# Revit family: TCNHBLE_with_1X2_Mixing_Box
name_source: partatom
category: Mechanical Equipment
units: mm (PartAtom-declared; Revit-internal decimal feet)

## family parameters
Always vertical = Yes
Cut with Voids When Loaded = No
Part Type = Normal
Room Calculation Point = No
Round Connector Dimension = Use Diameter
Shared = No
Work Plane-Based = No

## types (34) — shared parameters
0 = 0"
1" = 1"
1.5 = 1 1/2"
135 = 135.00°
2" = 2"
2' = 24"
3" = 3"
3.125" = 3 1/8"
4" = 4"
5" = 5"
Manufacturer = Loren Cook Company
Model = TCNHBLE-1X2_Mixing Box
ONE EIGTH = 1/8"
Type Comments = Tubular Centrifugal Inline Upblast Roof Mounted Arrangement 9 With 1X2 Mixing Box
URL = www.lorencook.com

## per-type parameters (varying)
- 100_TCNHBLE_1x2_ENDS: ((E - MIXING_BOX_HEIGHT - 0'  5") * 0.8)=19 19/32"; (C/2)+.125"=12 1/8"; (C/2)+.5"=-11 1/2"; (C/2)-.5"=-12 1/2"; -((E - MIXING_BOX_HEIGHT - 0'  5") * 0.8)=-19 19/32"; -B=-23 1/16"; -B/2=-11 17/32"; -C=-24"; A=120"; A-C-D=41"; B=23 1/16"; B/2=11 17/32"; C=24"; C+.25"=24 1/4"; C/2=30"; D=34"; DUAL_F=51"; DUAL_F+.5"=51 1/2"; DUAL_F/2=25 1/2"; E=60"; F=20"; F-1"=19"; FAN_DIA=16"; FAN_DIA-(C/2)=4"; FAN_RAD=8"; FAN_RAD*.33=5 9/32"; FAN_RAD*.8=4 13/16"; FAN_RAD+4"=12"; LONG_RO=44 1/16"; MB/2=15 1/4"; MIXING_BOX_HEIGHT=30 1/2"; MIXING_BOX_HEIGHT+.125"=30 5/8"; MIXING_BOX_HEIGHT-2.875"=27 5/8"; RO=16 13/16"; RO/2=8 13/32"; TYPE=12"
- 120_TCNHBLE_1x2_ENDS: ((E - MIXING_BOX_HEIGHT - 0'  5") * 0.8)=20 13/32"; (C/2)+.125"=14 1/8"; (C/2)+.5"=-13 1/2"; (C/2)-.5"=-14 1/2"; -((E - MIXING_BOX_HEIGHT - 0'  5") * 0.8)=-20 13/32"; -B=-27 1/16"; -B/2=-13 17/32"; -C=-28"; A=120"; A-C-D=37"; B=27 1/16"; B/2=13 17/32"; C=28"; C+.25"=28 1/4"; C/2=31"; D=38"; DUAL_F=59"; DUAL_F+.5"=59 1/2"; DUAL_F/2=29 1/2"; E=62"; F=22"; F-1"=21"; FAN_DIA=18"; FAN_DIA-(C/2)=4"; FAN_RAD=9"; FAN_RAD*.33=5 15/16"; FAN_RAD*.8=5 13/32"; FAN_RAD+4"=13"; LONG_RO=52 1/16"; MB/2=15 3/4"; MIXING_BOX_HEIGHT=31 1/2"; MIXING_BOX_HEIGHT+.125"=31 5/8"; MIXING_BOX_HEIGHT-2.875"=28 5/8"; RO=20 13/16"; RO/2=10 13/32"; TYPE=12"
- 135_TCNHBLE_1x2_ENDS: ((E - MIXING_BOX_HEIGHT - 0'  5") * 0.8)=21"; (C/2)+.125"=15 1/8"; (C/2)+.5"=-14 1/2"; (C/2)-.5"=-15 1/2"; -((E - MIXING_BOX_HEIGHT - 0'  5") * 0.8)=-21"; -B=-29"; -B/2=-14 1/2"; -C=-30"; A=120"; A-C-D=32"; B=29"; B/2=14 1/2"; C=30"; C+.25"=30 1/4"; C/2=31 1/2"; D=40"; DUAL_F=63"; DUAL_F+.5"=63 1/2"; DUAL_F/2=31 1/2"; E=63"; F=26"; F-1"=25"; FAN_DIA=21"; FAN_DIA-(C/2)=6"; FAN_RAD=10 1/2"; FAN_RAD*.33=6 15/16"; FAN_RAD*.8=6 5/16"; FAN_RAD+4"=14 1/2"; LONG_RO=56 1/16"; MB/2=15 7/8"; MIXING_BOX_HEIGHT=31 3/4"; MIXING_BOX_HEIGHT+.125"=31 7/8"; MIXING_BOX_HEIGHT-2.875"=28 7/8"; RO=22 3/4"; RO/2=11 3/8"; TYPE=12"
- 150_TCNHBLE_1x2_ENDS: ((E - MIXING_BOX_HEIGHT - 0'  5") * 0.8)=23 19/32"; (C/2)+.125"=16 1/8"; (C/2)+.5"=-15 1/2"; (C/2)-.5"=-16 1/2"; -((E - MIXING_BOX_HEIGHT - 0'  5") * 0.8)=-23 19/32"; -B=-31"; -B/2=-15 1/2"; -C=-32"; A=120"; A-C-D=25"; B=31"; B/2=15 1/2"; C=32"; C+.25"=32 1/4"; C/2=33 1/2"; D=42"; DUAL_F=67"; DUAL_F+.5"=67 1/2"; DUAL_F/2=33 1/2"; E=67"; F=29"; F-1"=28"; FAN_DIA=24"; FAN_DIA-(C/2)=8"; FAN_RAD=12"; FAN_RAD*.33=7 29/32"; FAN_RAD*.8=7 3/16"; FAN_RAD+4"=16"; LONG_RO=60 1/16"; MB/2=16 1/4"; MIXING_BOX_HEIGHT=32 1/2"; MIXING_BOX_HEIGHT+.125"=32 5/8"; MIXING_BOX_HEIGHT-2.875"=29 5/8"; RO=24 3/4"; RO/2=12 3/8"; TYPE=12"
- 165_TCNHBLE_1x2_ENDS: ((E - MIXING_BOX_HEIGHT - 0'  5") * 0.8)=24 13/16"; (C/2)+.125"=17 1/8"; (C/2)+.5"=-16 1/2"; (C/2)-.5"=-17 1/2"; -((E - MIXING_BOX_HEIGHT - 0'  5") * 0.8)=-24 13/16"; -B=-33"; -B/2=-16 1/2"; -C=-34"; A=120"; A-C-D=21"; B=33"; B/2=16 1/2"; C=34"; C+.25"=34 1/4"; C/2=35"; D=46"; DUAL_F=71"; DUAL_F+.5"=71 1/2"; DUAL_F/2=35 1/2"; E=70"; F=30"; F-1"=29"; FAN_DIA=26"; FAN_DIA-(C/2)=9"; FAN_RAD=13"; FAN_RAD*.33=8 19/32"; FAN_RAD*.8=7 13/16"; FAN_RAD+4"=17"; LONG_RO=64 1/16"; MB/2=17"; MIXING_BOX_HEIGHT=34"; MIXING_BOX_HEIGHT+.125"=34 1/8"; MIXING_BOX_HEIGHT-2.875"=31 1/8"; RO=26 3/4"; RO/2=13 3/8"; TYPE=12"
- 180_TCNHBLE_1x2_ENDS: ((E - MIXING_BOX_HEIGHT - 0'  5") * 0.8)=26 13/32"; (C/2)+.125"=19 1/8"; (C/2)+.5"=-18 1/2"; (C/2)-.5"=-19 1/2"; -((E - MIXING_BOX_HEIGHT - 0'  5") * 0.8)=-26 13/32"; -B=-36 7/8"; -B/2=-18 7/16"; -C=-38"; A=120"; A-C-D=13"; B=36 7/8"; B/2=18 7/16"; C=38"; C+.25"=38 1/4"; C/2=36 1/2"; D=50"; DUAL_F=79"; DUAL_F+.5"=79 1/2"; DUAL_F/2=39 1/2"; E=73"; F=35"; F-1"=34"; FAN_DIA=28"; FAN_DIA-(C/2)=9"; FAN_RAD=14"; FAN_RAD*.33=9 1/4"; FAN_RAD*.8=8 13/32"; FAN_RAD+4"=18"; LONG_RO=71 13/16"; MB/2=17 1/2"; MIXING_BOX_HEIGHT=35"; MIXING_BOX_HEIGHT+.125"=35 1/8"; MIXING_BOX_HEIGHT-2.875"=32 1/8"; RO=30 5/8"; RO/2=15 5/16"; TYPE=12"
- 195_TCNHBLE_1x2_ENDS: ((E - MIXING_BOX_HEIGHT - 0'  5") * 0.8)=28 3/16"; (C/2)+.125"=21 1/8"; (C/2)+.5"=-20 1/2"; (C/2)-.5"=-21 1/2"; -((E - MIXING_BOX_HEIGHT - 0'  5") * 0.8)=-28 3/16"; -B=-40 7/8"; -B/2=-20 7/16"; -C=-42"; A=120"; A-C-D=6"; B=40 7/8"; B/2=20 7/16"; C=42"; C+.25"=42 1/4"; C/2=38"; D=54"; DUAL_F=87"; DUAL_F+.5"=87 1/2"; DUAL_F/2=43 1/2"; E=76"; F=39"; F-1"=38"; FAN_DIA=31"; FAN_DIA-(C/2)=10"; FAN_RAD=15 1/2"; FAN_RAD*.33=10 7/32"; FAN_RAD*.8=9 5/16"; FAN_RAD+4"=19 1/2"; LONG_RO=79 15/16"; MB/2=17 7/8"; MIXING_BOX_HEIGHT=35 3/4"; MIXING_BOX_HEIGHT+.125"=35 7/8"; MIXING_BOX_HEIGHT-2.875"=32 7/8"; RO=34 11/16"; RO/2=17 11/32"; TYPE=12"
- 210_TCNHBLE_1x2_ENDS: ((E - MIXING_BOX_HEIGHT - 0'  5") * 0.8)=29 3/16"; (C/2)+.125"=22 1/8"; (C/2)+.5"=-21 1/2"; (C/2)-.5"=-22 1/2"; -((E - MIXING_BOX_HEIGHT - 0'  5") * 0.8)=-29 3/16"; -B=-42 7/8"; -B/2=-21 7/16"; -C=-44"; A=124"; A-C-D=7"; B=42 7/8"; B/2=21 7/16"; C=44"; C+.25"=44 1/4"; C/2=38"; D=56"; DUAL_F=91"; DUAL_F+.5"=91 1/2"; DUAL_F/2=45 1/2"; E=76"; F=42"; F-1"=41"; FAN_DIA=34"; FAN_DIA-(C/2)=12"; FAN_RAD=17"; FAN_RAD*.33=11 7/32"; FAN_RAD*.8=10 3/16"; FAN_RAD+4"=21"; LONG_RO=83 15/16"; MB/2=17 1/4"; MIXING_BOX_HEIGHT=34 1/2"; MIXING_BOX_HEIGHT+.125"=34 5/8"; MIXING_BOX_HEIGHT-2.875"=31 5/8"; RO=36 11/16"; RO/2=18 11/32"; TYPE=12"
- 225_TCNHBLE_1x2_ENDS: ((E - MIXING_BOX_HEIGHT - 0'  5") * 0.8)=30 3/16"; (C/2)+.125"=24 1/8"; (C/2)+.5"=-23 1/2"; (C/2)-.5"=-24 1/2"; -((E - MIXING_BOX_HEIGHT - 0'  5") * 0.8)=-30 3/16"; -B=-46 7/8"; -B/2=-23 7/16"; -C=-48"; A=121 1/2"; A-C-D=1/2"; B=46 7/8"; B/2=23 7/16"; C=48"; C+.25"=48 1/4"; C/2=39"; D=60"; DUAL_F=99"; DUAL_F+.5"=99 1/2"; DUAL_F/2=49 1/2"; E=78"; F=44"; F-1"=43"; FAN_DIA=36"; FAN_DIA-(C/2)=12"; FAN_RAD=18"; FAN_RAD*.33=11 7/8"; FAN_RAD*.8=10 13/16"; FAN_RAD+4"=22"; LONG_RO=91 15/16"; MB/2=17 5/8"; MIXING_BOX_HEIGHT=35 1/4"; MIXING_BOX_HEIGHT+.125"=35 3/8"; MIXING_BOX_HEIGHT-2.875"=32 3/8"; RO=40 11/16"; RO/2=20 11/32"; TYPE=12"
- 245_TCNHBLE_1x2_ENDS: ((E - MIXING_BOX_HEIGHT - 0'  5") * 0.8)=34"; (C/2)+.125"=25 1/8"; (C/2)+.5"=-24 1/2"; (C/2)-.5"=-25 1/2"; -((E - MIXING_BOX_HEIGHT - 0'  5") * 0.8)=-34"; -B=-48 7/8"; -B/2=-24 7/16"; -C=-50"; A=135"; A-C-D=1"; B=48 7/8"; B/2=24 7/16"; C=50"; C+.25"=50 1/4"; C/2=42 1/2"; D=63"; DUAL_F=103"; DUAL_F+.5"=103 1/2"; DUAL_F/2=51 1/2"; E=85"; F=50"; F-1"=49"; FAN_DIA=40"; FAN_DIA-(C/2)=15"; FAN_RAD=20"; FAN_RAD*.33=13 3/16"; FAN_RAD*.8=12"; FAN_RAD+4"=24"; LONG_RO=95 15/16"; MB/2=18 3/4"; MIXING_BOX_HEIGHT=37 1/2"; MIXING_BOX_HEIGHT+.125"=37 5/8"; MIXING_BOX_HEIGHT-2.875"=34 5/8"; RO=42 11/16"; RO/2=21 11/32"; TYPE=12"
- 270_TCNHBLE_1x2_ENDS: ((E - MIXING_BOX_HEIGHT - 0'  5") * 0.8)=38 13/16"; (C/2)+.125"=27 1/8"; (C/2)+.5"=-26 1/2"; (C/2)-.5"=-27 1/2"; -((E - MIXING_BOX_HEIGHT - 0'  5") * 0.8)=-38 13/16"; -B=-52 7/8"; -B/2=-26 7/16"; -C=-54"; A=146 3/4"; A-C-D=3/4"; B=52 7/8"; B/2=26 7/16"; C=54"; C+.25"=54 1/4"; C/2=45 1/2"; D=67"; DUAL_F=111"; DUAL_F+.5"=111 1/2"; DUAL_F/2=55 1/2"; E=91"; F=56"; F-1"=55"; FAN_DIA=44"; FAN_DIA-(C/2)=17"; FAN_RAD=22"; FAN_RAD*.33=14 17/32"; FAN_RAD*.8=13 3/16"; FAN_RAD+4"=26"; LONG_RO=103 15/16"; MB/2=18 3/4"; MIXING_BOX_HEIGHT=37 1/2"; MIXING_BOX_HEIGHT+.125"=37 5/8"; MIXING_BOX_HEIGHT-2.875"=34 5/8"; RO=46 11/16"; RO/2=23 11/32"; TYPE=12"
- 300_TCNHBLE_1x2_ENDS: ((E - MIXING_BOX_HEIGHT - 0'  5") * 0.8)=39 13/16"; (C/2)+.125"=30 1/8"; (C/2)+.5"=-29 1/2"; (C/2)-.5"=-30 1/2"; -((E - MIXING_BOX_HEIGHT - 0'  5") * 0.8)=-39 13/16"; -B=-58 7/8"; -B/2=-29 7/16"; -C=-60"; A=153"; A-C-D=1"; B=58 7/8"; B/2=29 7/16"; C=60"; C+.25"=60 1/4"; C/2=46 1/2"; D=74"; DUAL_F=123"; DUAL_F+.5"=123 1/2"; DUAL_F/2=61 1/2"; E=93"; F=60"; F-1"=59"; FAN_DIA=48"; FAN_DIA-(C/2)=18"; FAN_RAD=24"; FAN_RAD*.33=15 27/32"; FAN_RAD*.8=14 13/32"; FAN_RAD+4"=28"; LONG_RO=115 15/16"; MB/2=19 1/8"; MIXING_BOX_HEIGHT=38 1/4"; MIXING_BOX_HEIGHT+.125"=38 3/8"; MIXING_BOX_HEIGHT-2.875"=35 3/8"; RO=52 11/16"; RO/2=26 11/32"; TYPE=12"
- 330_TCNHBLE_1x2_ENDS: ((E - MIXING_BOX_HEIGHT - 0'  5") * 0.8)=42 13/16"; (C/2)+.125"=31 1/8"; (C/2)+.5"=-30 1/2"; (C/2)-.5"=-31 1/2"; -((E - MIXING_BOX_HEIGHT - 0'  5") * 0.8)=-42 13/16"; -B=-60 3/4"; -B/2=-30 3/8"; -C=-62"; A=164 1/4"; A-C-D=1 1/4"; B=60 3/4"; B/2=30 3/8"; C=62"; C+.25"=62 1/4"; C/2=50"; D=77"; DUAL_F=127"; DUAL_F+.5"=127 1/2"; DUAL_F/2=63 1/2"; E=100"; F=64"; F-1"=63"; FAN_DIA=52"; FAN_DIA-(C/2)=21"; FAN_RAD=26"; FAN_RAD*.33=17 5/32"; FAN_RAD*.8=15 19/32"; FAN_RAD+4"=30"; LONG_RO=119 13/16"; MB/2=20 3/4"; MIXING_BOX_HEIGHT=41 1/2"; MIXING_BOX_HEIGHT+.125"=41 5/8"; MIXING_BOX_HEIGHT-2.875"=38 5/8"; RO=54 9/16"; RO/2=27 9/32"; TYPE=12"
- 365_TCNHBLE_1x2_ENDS: ((E - MIXING_BOX_HEIGHT - 0'  5") * 0.8)=44 19/32"; (C/2)+.125"=32 5/8"; (C/2)+.5"=-32"; (C/2)-.5"=-33"; -((E - MIXING_BOX_HEIGHT - 0'  5") * 0.8)=-44 19/32"; -B=-63 3/4"; -B/2=-31 7/8"; -C=-65"; A=170"; A-C-D=1"; B=63 3/4"; B/2=31 7/8"; C=65"; C+.25"=65 1/4"; C/2=52 1/2"; D=82"; DUAL_F=133"; DUAL_F+.5"=133 1/2"; DUAL_F/2=66 1/2"; E=105"; F=65"; F-1"=64"; FAN_DIA=54"; FAN_DIA-(C/2)=21 1/2"; FAN_RAD=27"; FAN_RAD*.33=17 13/16"; FAN_RAD*.8=16 3/16"; FAN_RAD+4"=31"; LONG_RO=125 13/16"; MB/2=22 1/8"; MIXING_BOX_HEIGHT=44 1/4"; MIXING_BOX_HEIGHT+.125"=44 3/8"; MIXING_BOX_HEIGHT-2.875"=41 3/8"; RO=57 9/16"; RO/2=28 25/32"; TYPE=12"
- 402_TCNHBLE_1x2_ENDS: ((E - MIXING_BOX_HEIGHT - 0'  5") * 0.8)=49 3/16"; (C/2)+.125"=36 1/8"; (C/2)+.5"=-35 1/2"; (C/2)-.5"=-36 1/2"; -((E - MIXING_BOX_HEIGHT - 0'  5") * 0.8)=-49 3/16"; -B=-70 3/4"; -B/2=-35 3/8"; -C=-72"; A=184 3/4"; A-C-D=3/4"; B=70 3/4"; B/2=35 3/8"; C=72"; C+.25"=72 1/4"; C/2=56 1/2"; D=90"; DUAL_F=147"; DUAL_F+.5"=147 1/2"; DUAL_F/2=73 1/2"; E=113"; F=72"; F-1"=71"; FAN_DIA=60"; FAN_DIA-(C/2)=24"; FAN_RAD=30"; FAN_RAD*.33=19 13/16"; FAN_RAD*.8=18"; FAN_RAD+4"=34"; LONG_RO=139 13/16"; MB/2=23 1/4"; MIXING_BOX_HEIGHT=46 1/2"; MIXING_BOX_HEIGHT+.125"=46 5/8"; MIXING_BOX_HEIGHT-2.875"=43 5/8"; RO=64 9/16"; RO/2=32 9/32"; TYPE=12"
- 445_TCNHBLE_1x2_ENDS: ((E - MIXING_BOX_HEIGHT - 0'  5") * 0.8)=54 3/16"; (C/2)+.125"=38 5/8"; (C/2)+.5"=-38"; (C/2)-.5"=-39"; -((E - MIXING_BOX_HEIGHT - 0'  5") * 0.8)=-54 3/16"; -B=-75 3/4"; -B/2=-37 7/8"; -C=-77"; A=206"; A-C-D=1"; B=75 3/4"; B/2=37 7/8"; C=77"; C+.25"=77 1/4"; C/2=63"; D=98"; DUAL_F=157"; DUAL_F+.5"=157 1/2"; DUAL_F/2=78 1/2"; E=126"; F=80"; F-1"=79"; FAN_DIA=66"; FAN_DIA-(C/2)=27 1/2"; FAN_RAD=33"; FAN_RAD*.33=21 25/32"; FAN_RAD*.8=19 13/16"; FAN_RAD+4"=37"; LONG_RO=149 13/16"; MB/2=26 5/8"; MIXING_BOX_HEIGHT=53 1/4"; MIXING_BOX_HEIGHT+.125"=53 3/8"; MIXING_BOX_HEIGHT-2.875"=50 3/8"; RO=69 9/16"; RO/2=34 25/32"; TYPE=12"
- 490_TCNHBLE_1x2_ENDS: ((E - MIXING_BOX_HEIGHT - 0'  5") * 0.8)=59 13/16"; (C/2)+.125"=42 1/8"; (C/2)+.5"=-41 1/2"; (C/2)-.5"=-42 1/2"; -((E - MIXING_BOX_HEIGHT - 0'  5") * 0.8)=-59 13/16"; -B=-82 3/4"; -B/2=-41 3/8"; -C=-84"; A=225 1/2"; A-C-D=1/2"; B=82 3/4"; B/2=41 3/8"; C=84"; C+.25"=84 1/4"; C/2=69 1/2"; D=108"; DUAL_F=171"; DUAL_F+.5"=171 1/2"; DUAL_F/2=85 1/2"; E=139"; F=87"; F-1"=86"; FAN_DIA=73"; FAN_DIA-(C/2)=31"; FAN_RAD=36 1/2"; FAN_RAD*.33=24 3/32"; FAN_RAD*.8=21 29/32"; FAN_RAD+4"=40 1/2"; LONG_RO=163 13/16"; MB/2=29 5/8"; MIXING_BOX_HEIGHT=59 1/4"; MIXING_BOX_HEIGHT+.125"=59 3/8"; MIXING_BOX_HEIGHT-2.875"=56 3/8"; RO=76 1/2"; RO/2=38 1/4"; TYPE=12"
- 100_TCNHBLE_1x2_SIDES: ((E - MIXING_BOX_HEIGHT - 0'  5") * 0.8)=19 19/32"; (C/2)+.125"=12 1/8"; (C/2)+.5"=-11 1/2"; (C/2)-.5"=-12 1/2"; -((E - MIXING_BOX_HEIGHT - 0'  5") * 0.8)=-19 19/32"; -B=-23 1/16"; -B/2=-11 17/32"; -C=-24"; A=120"; A-C-D=41"; B=23 1/16"; B/2=11 17/32"; C=24"; C+.25"=24 1/4"; C/2=30"; D=34"; DUAL_F=51"; DUAL_F+.5"=51 1/2"; DUAL_F/2=25 1/2"; E=60"; F=20"; F-1"=19"; FAN_DIA=16"; FAN_DIA-(C/2)=4"; FAN_RAD=8"; FAN_RAD*.33=5 9/32"; FAN_RAD*.8=4 13/16"; FAN_RAD+4"=12"; LONG_RO=44 1/16"; MB/2=15 1/4"; MIXING_BOX_HEIGHT=30 1/2"; MIXING_BOX_HEIGHT+.125"=30 5/8"; MIXING_BOX_HEIGHT-2.875"=27 5/8"; RO=16 13/16"; RO/2=8 13/32"; TYPE=24"
- 120_TCNHBLE_1x2_SIDES: ((E - MIXING_BOX_HEIGHT - 0'  5") * 0.8)=20 13/32"; (C/2)+.125"=14 1/8"; (C/2)+.5"=-13 1/2"; (C/2)-.5"=-14 1/2"; -((E - MIXING_BOX_HEIGHT - 0'  5") * 0.8)=-20 13/32"; -B=-27 1/16"; -B/2=-13 17/32"; -C=-28"; A=120"; A-C-D=37"; B=27 1/16"; B/2=13 17/32"; C=28"; C+.25"=28 1/4"; C/2=31"; D=38"; DUAL_F=59"; DUAL_F+.5"=59 1/2"; DUAL_F/2=29 1/2"; E=62"; F=22"; F-1"=21"; FAN_DIA=18"; FAN_DIA-(C/2)=4"; FAN_RAD=9"; FAN_RAD*.33=5 15/16"; FAN_RAD*.8=5 13/32"; FAN_RAD+4"=13"; LONG_RO=52 1/16"; MB/2=15 3/4"; MIXING_BOX_HEIGHT=31 1/2"; MIXING_BOX_HEIGHT+.125"=31 5/8"; MIXING_BOX_HEIGHT-2.875"=28 5/8"; RO=20 13/16"; RO/2=10 13/32"; TYPE=24"
- 135_TCNHBLE_1x2_SIDES: ((E - MIXING_BOX_HEIGHT - 0'  5") * 0.8)=21"; (C/2)+.125"=15 1/8"; (C/2)+.5"=-14 1/2"; (C/2)-.5"=-15 1/2"; -((E - MIXING_BOX_HEIGHT - 0'  5") * 0.8)=-21"; -B=-29"; -B/2=-14 1/2"; -C=-30"; A=120"; A-C-D=32"; B=29"; B/2=14 1/2"; C=30"; C+.25"=30 1/4"; C/2=31 1/2"; D=40"; DUAL_F=63"; DUAL_F+.5"=63 1/2"; DUAL_F/2=31 1/2"; E=63"; F=26"; F-1"=25"; FAN_DIA=21"; FAN_DIA-(C/2)=6"; FAN_RAD=10 1/2"; FAN_RAD*.33=6 15/16"; FAN_RAD*.8=6 5/16"; FAN_RAD+4"=14 1/2"; LONG_RO=56 1/16"; MB/2=15 7/8"; MIXING_BOX_HEIGHT=31 3/4"; MIXING_BOX_HEIGHT+.125"=31 7/8"; MIXING_BOX_HEIGHT-2.875"=28 7/8"; RO=22 3/4"; RO/2=11 3/8"; TYPE=24"
- 150_TCNHBLE_1x2_SIDES: ((E - MIXING_BOX_HEIGHT - 0'  5") * 0.8)=23 19/32"; (C/2)+.125"=16 1/8"; (C/2)+.5"=-15 1/2"; (C/2)-.5"=-16 1/2"; -((E - MIXING_BOX_HEIGHT - 0'  5") * 0.8)=-23 19/32"; -B=-31"; -B/2=-15 1/2"; -C=-32"; A=120"; A-C-D=25"; B=31"; B/2=15 1/2"; C=32"; C+.25"=32 1/4"; C/2=33 1/2"; D=42"; DUAL_F=67"; DUAL_F+.5"=67 1/2"; DUAL_F/2=33 1/2"; E=67"; F=29"; F-1"=28"; FAN_DIA=24"; FAN_DIA-(C/2)=8"; FAN_RAD=12"; FAN_RAD*.33=7 29/32"; FAN_RAD*.8=7 3/16"; FAN_RAD+4"=16"; LONG_RO=60 1/16"; MB/2=16 1/4"; MIXING_BOX_HEIGHT=32 1/2"; MIXING_BOX_HEIGHT+.125"=32 5/8"; MIXING_BOX_HEIGHT-2.875"=29 5/8"; RO=24 3/4"; RO/2=12 3/8"; TYPE=24"
- 165_TCNHBLE_1x2_SIDES: ((E - MIXING_BOX_HEIGHT - 0'  5") * 0.8)=24 13/16"; (C/2)+.125"=17 1/8"; (C/2)+.5"=-16 1/2"; (C/2)-.5"=-17 1/2"; -((E - MIXING_BOX_HEIGHT - 0'  5") * 0.8)=-24 13/16"; -B=-33"; -B/2=-16 1/2"; -C=-34"; A=120"; A-C-D=21"; B=33"; B/2=16 1/2"; C=34"; C+.25"=34 1/4"; C/2=35"; D=46"; DUAL_F=71"; DUAL_F+.5"=71 1/2"; DUAL_F/2=35 1/2"; E=70"; F=30"; F-1"=29"; FAN_DIA=26"; FAN_DIA-(C/2)=9"; FAN_RAD=13"; FAN_RAD*.33=8 19/32"; FAN_RAD*.8=7 13/16"; FAN_RAD+4"=17"; LONG_RO=64 1/16"; MB/2=17"; MIXING_BOX_HEIGHT=34"; MIXING_BOX_HEIGHT+.125"=34 1/8"; MIXING_BOX_HEIGHT-2.875"=31 1/8"; RO=26 3/4"; RO/2=13 3/8"; TYPE=24"
- 180_TCNHBLE_1x2_SIDES: ((E - MIXING_BOX_HEIGHT - 0'  5") * 0.8)=26 13/32"; (C/2)+.125"=19 1/8"; (C/2)+.5"=-18 1/2"; (C/2)-.5"=-19 1/2"; -((E - MIXING_BOX_HEIGHT - 0'  5") * 0.8)=-26 13/32"; -B=-36 7/8"; -B/2=-18 7/16"; -C=-38"; A=120"; A-C-D=13"; B=36 7/8"; B/2=18 7/16"; C=38"; C+.25"=38 1/4"; C/2=36 1/2"; D=50"; DUAL_F=79"; DUAL_F+.5"=79 1/2"; DUAL_F/2=39 1/2"; E=73"; F=35"; F-1"=34"; FAN_DIA=28"; FAN_DIA-(C/2)=9"; FAN_RAD=14"; FAN_RAD*.33=9 1/4"; FAN_RAD*.8=8 13/32"; FAN_RAD+4"=18"; LONG_RO=71 13/16"; MB/2=17 1/2"; MIXING_BOX_HEIGHT=35"; MIXING_BOX_HEIGHT+.125"=35 1/8"; MIXING_BOX_HEIGHT-2.875"=32 1/8"; RO=30 5/8"; RO/2=15 5/16"; TYPE=24"
- 195_TCNHBLE_1x2_SIDES: ((E - MIXING_BOX_HEIGHT - 0'  5") * 0.8)=28 3/16"; (C/2)+.125"=21 1/8"; (C/2)+.5"=-20 1/2"; (C/2)-.5"=-21 1/2"; -((E - MIXING_BOX_HEIGHT - 0'  5") * 0.8)=-28 3/16"; -B=-40 7/8"; -B/2=-20 7/16"; -C=-42"; A=120"; A-C-D=6"; B=40 7/8"; B/2=20 7/16"; C=42"; C+.25"=42 1/4"; C/2=38"; D=54"; DUAL_F=87"; DUAL_F+.5"=87 1/2"; DUAL_F/2=43 1/2"; E=76"; F=39"; F-1"=38"; FAN_DIA=31"; FAN_DIA-(C/2)=10"; FAN_RAD=15 1/2"; FAN_RAD*.33=10 7/32"; FAN_RAD*.8=9 5/16"; FAN_RAD+4"=19 1/2"; LONG_RO=79 15/16"; MB/2=17 7/8"; MIXING_BOX_HEIGHT=35 3/4"; MIXING_BOX_HEIGHT+.125"=35 7/8"; MIXING_BOX_HEIGHT-2.875"=32 7/8"; RO=34 11/16"; RO/2=17 11/32"; TYPE=24"
- 210_TCNHBLE_1x2_SIDES: ((E - MIXING_BOX_HEIGHT - 0'  5") * 0.8)=29 3/16"; (C/2)+.125"=22 1/8"; (C/2)+.5"=-21 1/2"; (C/2)-.5"=-22 1/2"; -((E - MIXING_BOX_HEIGHT - 0'  5") * 0.8)=-29 3/16"; -B=-42 7/8"; -B/2=-21 7/16"; -C=-44"; A=124"; A-C-D=7"; B=42 7/8"; B/2=21 7/16"; C=44"; C+.25"=44 1/4"; C/2=38"; D=56"; DUAL_F=91"; DUAL_F+.5"=91 1/2"; DUAL_F/2=45 1/2"; E=76"; F=42"; F-1"=41"; FAN_DIA=34"; FAN_DIA-(C/2)=12"; FAN_RAD=17"; FAN_RAD*.33=11 7/32"; FAN_RAD*.8=10 3/16"; FAN_RAD+4"=21"; LONG_RO=83 15/16"; MB/2=17 1/4"; MIXING_BOX_HEIGHT=34 1/2"; MIXING_BOX_HEIGHT+.125"=34 5/8"; MIXING_BOX_HEIGHT-2.875"=31 5/8"; RO=36 11/16"; RO/2=18 11/32"; TYPE=24"
- 225_TCNHBLE_1x2_SIDES: ((E - MIXING_BOX_HEIGHT - 0'  5") * 0.8)=30 3/16"; (C/2)+.125"=24 1/8"; (C/2)+.5"=-23 1/2"; (C/2)-.5"=-24 1/2"; -((E - MIXING_BOX_HEIGHT - 0'  5") * 0.8)=-30 3/16"; -B=-46 7/8"; -B/2=-23 7/16"; -C=-48"; A=121 1/2"; A-C-D=1/2"; B=46 7/8"; B/2=23 7/16"; C=48"; C+.25"=48 1/4"; C/2=39"; D=60"; DUAL_F=99"; DUAL_F+.5"=99 1/2"; DUAL_F/2=49 1/2"; E=78"; F=44"; F-1"=43"; FAN_DIA=36"; FAN_DIA-(C/2)=12"; FAN_RAD=18"; FAN_RAD*.33=11 7/8"; FAN_RAD*.8=10 13/16"; FAN_RAD+4"=22"; LONG_RO=91 15/16"; MB/2=17 5/8"; MIXING_BOX_HEIGHT=35 1/4"; MIXING_BOX_HEIGHT+.125"=35 3/8"; MIXING_BOX_HEIGHT-2.875"=32 3/8"; RO=40 11/16"; RO/2=20 11/32"; TYPE=24"
- 245_TCNHBLE_1x2_SIDES: ((E - MIXING_BOX_HEIGHT - 0'  5") * 0.8)=34"; (C/2)+.125"=25 1/8"; (C/2)+.5"=-24 1/2"; (C/2)-.5"=-25 1/2"; -((E - MIXING_BOX_HEIGHT - 0'  5") * 0.8)=-34"; -B=-48 7/8"; -B/2=-24 7/16"; -C=-50"; A=135"; A-C-D=1"; B=48 7/8"; B/2=24 7/16"; C=50"; C+.25"=50 1/4"; C/2=42 1/2"; D=63"; DUAL_F=103"; DUAL_F+.5"=103 1/2"; DUAL_F/2=51 1/2"; E=85"; F=50"; F-1"=49"; FAN_DIA=40"; FAN_DIA-(C/2)=15"; FAN_RAD=20"; FAN_RAD*.33=13 3/16"; FAN_RAD*.8=12"; FAN_RAD+4"=24"; LONG_RO=95 15/16"; MB/2=18 3/4"; MIXING_BOX_HEIGHT=37 1/2"; MIXING_BOX_HEIGHT+.125"=37 5/8"; MIXING_BOX_HEIGHT-2.875"=34 5/8"; RO=42 11/16"; RO/2=21 11/32"; TYPE=24"
- 270_TCNHBLE_1x2_SIDES: ((E - MIXING_BOX_HEIGHT - 0'  5") * 0.8)=38 13/16"; (C/2)+.125"=27 1/8"; (C/2)+.5"=-26 1/2"; (C/2)-.5"=-27 1/2"; -((E - MIXING_BOX_HEIGHT - 0'  5") * 0.8)=-38 13/16"; -B=-52 7/8"; -B/2=-26 7/16"; -C=-54"; A=146 3/4"; A-C-D=3/4"; B=52 7/8"; B/2=26 7/16"; C=54"; C+.25"=54 1/4"; C/2=45 1/2"; D=67"; DUAL_F=111"; DUAL_F+.5"=111 1/2"; DUAL_F/2=55 1/2"; E=91"; F=56"; F-1"=55"; FAN_DIA=44"; FAN_DIA-(C/2)=17"; FAN_RAD=22"; FAN_RAD*.33=14 17/32"; FAN_RAD*.8=13 3/16"; FAN_RAD+4"=26"; LONG_RO=103 15/16"; MB/2=18 3/4"; MIXING_BOX_HEIGHT=37 1/2"; MIXING_BOX_HEIGHT+.125"=37 5/8"; MIXING_BOX_HEIGHT-2.875"=34 5/8"; RO=46 11/16"; RO/2=23 11/32"; TYPE=24"
- 300_TCNHBLE_1x2_SIDES: ((E - MIXING_BOX_HEIGHT - 0'  5") * 0.8)=39 13/16"; (C/2)+.125"=30 1/8"; (C/2)+.5"=-29 1/2"; (C/2)-.5"=-30 1/2"; -((E - MIXING_BOX_HEIGHT - 0'  5") * 0.8)=-39 13/16"; -B=-58 7/8"; -B/2=-29 7/16"; -C=-60"; A=153"; A-C-D=1"; B=58 7/8"; B/2=29 7/16"; C=60"; C+.25"=60 1/4"; C/2=46 1/2"; D=74"; DUAL_F=123"; DUAL_F+.5"=123 1/2"; DUAL_F/2=61 1/2"; E=93"; F=60"; F-1"=59"; FAN_DIA=48"; FAN_DIA-(C/2)=18"; FAN_RAD=24"; FAN_RAD*.33=15 27/32"; FAN_RAD*.8=14 13/32"; FAN_RAD+4"=28"; LONG_RO=115 15/16"; MB/2=19 1/8"; MIXING_BOX_HEIGHT=38 1/4"; MIXING_BOX_HEIGHT+.125"=38 3/8"; MIXING_BOX_HEIGHT-2.875"=35 3/8"; RO=52 11/16"; RO/2=26 11/32"; TYPE=24"
- 330_TCNHBLE_1x2_SIDES: ((E - MIXING_BOX_HEIGHT - 0'  5") * 0.8)=42 13/16"; (C/2)+.125"=31 1/8"; (C/2)+.5"=-30 1/2"; (C/2)-.5"=-31 1/2"; -((E - MIXING_BOX_HEIGHT - 0'  5") * 0.8)=-42 13/16"; -B=-60 3/4"; -B/2=-30 3/8"; -C=-62"; A=164 1/4"; A-C-D=1 1/4"; B=60 3/4"; B/2=30 3/8"; C=62"; C+.25"=62 1/4"; C/2=50"; D=77"; DUAL_F=127"; DUAL_F+.5"=127 1/2"; DUAL_F/2=63 1/2"; E=100"; F=64"; F-1"=63"; FAN_DIA=52"; FAN_DIA-(C/2)=21"; FAN_RAD=26"; FAN_RAD*.33=17 5/32"; FAN_RAD*.8=15 19/32"; FAN_RAD+4"=30"; LONG_RO=119 13/16"; MB/2=20 3/4"; MIXING_BOX_HEIGHT=41 1/2"; MIXING_BOX_HEIGHT+.125"=41 5/8"; MIXING_BOX_HEIGHT-2.875"=38 5/8"; RO=54 9/16"; RO/2=27 9/32"; TYPE=24"
- 365_TCNHBLE_1x2_SIDES: ((E - MIXING_BOX_HEIGHT - 0'  5") * 0.8)=44 19/32"; (C/2)+.125"=32 5/8"; (C/2)+.5"=-32"; (C/2)-.5"=-33"; -((E - MIXING_BOX_HEIGHT - 0'  5") * 0.8)=-44 19/32"; -B=-63 3/4"; -B/2=-31 7/8"; -C=-65"; A=170"; A-C-D=1"; B=63 3/4"; B/2=31 7/8"; C=65"; C+.25"=65 1/4"; C/2=52 1/2"; D=82"; DUAL_F=133"; DUAL_F+.5"=133 1/2"; DUAL_F/2=66 1/2"; E=105"; F=65"; F-1"=64"; FAN_DIA=54"; FAN_DIA-(C/2)=21 1/2"; FAN_RAD=27"; FAN_RAD*.33=17 13/16"; FAN_RAD*.8=16 3/16"; FAN_RAD+4"=31"; LONG_RO=125 13/16"; MB/2=22 1/8"; MIXING_BOX_HEIGHT=44 1/4"; MIXING_BOX_HEIGHT+.125"=44 3/8"; MIXING_BOX_HEIGHT-2.875"=41 3/8"; RO=57 9/16"; RO/2=28 25/32"; TYPE=24"
- 402_TCNHBLE_1x2_SIDES: ((E - MIXING_BOX_HEIGHT - 0'  5") * 0.8)=49 3/16"; (C/2)+.125"=36 1/8"; (C/2)+.5"=-35 1/2"; (C/2)-.5"=-36 1/2"; -((E - MIXING_BOX_HEIGHT - 0'  5") * 0.8)=-49 3/16"; -B=-70 3/4"; -B/2=-35 3/8"; -C=-72"; A=184 3/4"; A-C-D=3/4"; B=70 3/4"; B/2=35 3/8"; C=72"; C+.25"=72 1/4"; C/2=56 1/2"; D=90"; DUAL_F=147"; DUAL_F+.5"=147 1/2"; DUAL_F/2=73 1/2"; E=113"; F=72"; F-1"=71"; FAN_DIA=60"; FAN_DIA-(C/2)=24"; FAN_RAD=30"; FAN_RAD*.33=19 13/16"; FAN_RAD*.8=18"; FAN_RAD+4"=34"; LONG_RO=139 13/16"; MB/2=23 1/4"; MIXING_BOX_HEIGHT=46 1/2"; MIXING_BOX_HEIGHT+.125"=46 5/8"; MIXING_BOX_HEIGHT-2.875"=43 5/8"; RO=64 9/16"; RO/2=32 9/32"; TYPE=24"
- 445_TCNHBLE_1x2_SIDES: ((E - MIXING_BOX_HEIGHT - 0'  5") * 0.8)=54 3/16"; (C/2)+.125"=38 5/8"; (C/2)+.5"=-38"; (C/2)-.5"=-39"; -((E - MIXING_BOX_HEIGHT - 0'  5") * 0.8)=-54 3/16"; -B=-75 3/4"; -B/2=-37 7/8"; -C=-77"; A=206"; A-C-D=1"; B=75 3/4"; B/2=37 7/8"; C=77"; C+.25"=77 1/4"; C/2=63"; D=98"; DUAL_F=157"; DUAL_F+.5"=157 1/2"; DUAL_F/2=78 1/2"; E=126"; F=80"; F-1"=79"; FAN_DIA=66"; FAN_DIA-(C/2)=27 1/2"; FAN_RAD=33"; FAN_RAD*.33=21 25/32"; FAN_RAD*.8=19 13/16"; FAN_RAD+4"=37"; LONG_RO=149 13/16"; MB/2=26 5/8"; MIXING_BOX_HEIGHT=53 1/4"; MIXING_BOX_HEIGHT+.125"=53 3/8"; MIXING_BOX_HEIGHT-2.875"=50 3/8"; RO=69 9/16"; RO/2=34 25/32"; TYPE=12"
- 490_TCNHBLE_1x2_SIDES: ((E - MIXING_BOX_HEIGHT - 0'  5") * 0.8)=59 13/16"; (C/2)+.125"=42 1/8"; (C/2)+.5"=-41 1/2"; (C/2)-.5"=-42 1/2"; -((E - MIXING_BOX_HEIGHT - 0'  5") * 0.8)=-59 13/16"; -B=-82 3/4"; -B/2=-41 3/8"; -C=-84"; A=225 1/2"; A-C-D=1/2"; B=82 3/4"; B/2=41 3/8"; C=84"; C+.25"=84 1/4"; C/2=69 1/2"; D=108"; DUAL_F=171"; DUAL_F+.5"=171 1/2"; DUAL_F/2=85 1/2"; E=139"; F=87"; F-1"=86"; FAN_DIA=73"; FAN_DIA-(C/2)=31"; FAN_RAD=36 1/2"; FAN_RAD*.33=24 3/32"; FAN_RAD*.8=21 29/32"; FAN_RAD+4"=40 1/2"; LONG_RO=163 13/16"; MB/2=29 5/8"; MIXING_BOX_HEIGHT=59 1/4"; MIXING_BOX_HEIGHT+.125"=59 3/8"; MIXING_BOX_HEIGHT-2.875"=56 3/8"; RO=76 1/2"; RO/2=38 1/4"; TYPE=12"

## geometry (parser evidence)
native form markers: Sweep x3
no freeform markers — native parametric forms only
